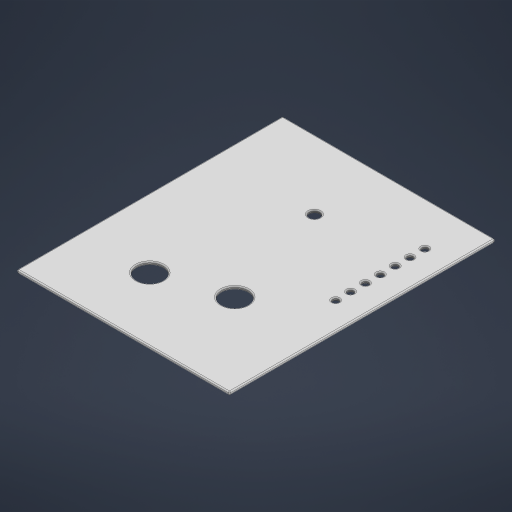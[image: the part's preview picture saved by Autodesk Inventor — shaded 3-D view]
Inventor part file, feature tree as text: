
AUTODESK INVENTOR PART (.ipt)
format: ipt  version: 2023 (Build 270158000, 158)  size: 272,896 bytes
history: native  units: mm
features: extrude x1, fillet x1, other x1
ambient origin geometry x8: Origin, YZ Plane, XZ Plane, XY Plane, X Axis, Y Axis, Z Axis, Center Point
bodies: Solid1 (feature_tree)
feature tree (3):
  extrude  "extra"  Depth=200.0mm
  fillet  "Fillet1"  Radius=250.0mm
  other  "page_lines"
